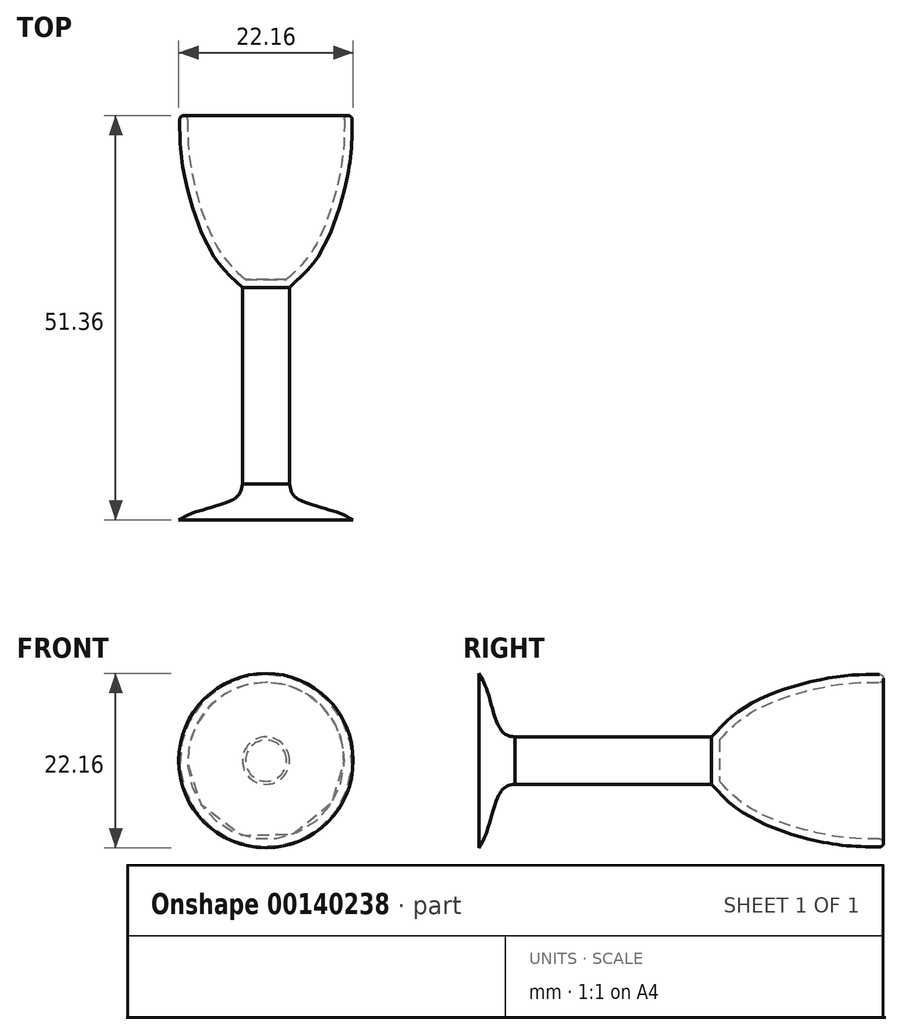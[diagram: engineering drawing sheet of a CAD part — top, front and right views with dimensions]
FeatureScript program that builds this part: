
annotation { "Feature Type Name" : "Feature", "Feature Type Description" : "" }
export const myFeature = defineFeature(function(context is Context, id is Id, definition is map)
    precondition{}
    {
        {
            var Q0;
            Q0=qCreatedBy(makeId("Top.planeOp"),FACE);
            var sketch = newSketch(context, id + "F0", { "sketchPlane" : qUnion([Q0])});
            skLineSegment(sketch, "E0", {"start": v(0, 0) * mm, "end": v(-3, 0) * mm});
            skLineSegment(sketch, "E1", {"start": v(0, 8.3) * mm, "end": v(0, 0) * mm});
            skFitSpline(sketch, "E2", {"points": [v(-3, 0) * mm, v(-6.5, 3.75) * mm, v(-9.46, 10.5) * mm, v(-10.81, 17.24) * mm, v(-10.95, 21.82) * mm], "startDerivative": vector(-15.82, 14.3) * mm, "endDerivative": vector(0.17, 19.93) * mm});
            skLineSegment(sketch, "E3", {"start": v(-10.95, 21.82) * mm, "end": v(0, 21.82) * mm});
            skLineSegment(sketch, "E4", {"start": v(0, 21.82) * mm, "end": v(0, 8.3) * mm});
            skSolve(sketch);
        }
        {
            var Q0;
            Q0=makeQuery(id+"F0.imprint","IMPRINT",FACE,{"disambiguationData":[TD([[makeQuery(id+"F0.imprint","IMPRINT",EDGE,{"derivedFrom":sQuery(id+"F0.wireOp",EDGE,"E0")}),-1.0]])]});
            var Q1;
            Q1=sQuery(id+"F0.wireOp",EDGE,"E1");
            revolve(context, id + "F1", {"entities" : qUnion([Q0]), "axis" : qUnion([Q1]), "revolveType" : RevolveType.FULL});
        }
        {
            var Q0;
            Q0=makeQuery(id+"F1.opRevolve","SWEPT_FACE",FACE,{"disambiguationData":[OSD([sQuery(id+"F0.wireOp",EDGE,"E0")])]});
            var sketch = newSketch(context, id + "F2", { "sketchPlane" : qUnion([Q0])});
            skCircle(sketch, "E5", {"center": v(0, 0) * mm, "radius": 3 * mm});
            skSolve(sketch);
        }
        {
            var Q0;
            Q0=makeQuery(id+"F1.opRevolve","SWEPT_FACE",FACE,{"disambiguationData":[OSD([sQuery(id+"F0.wireOp",EDGE,"E3")])]});
            shell(context, id + "F3", {"entities" : qUnion([Q0]), "thickness" : 1 * mm});
        }
        {
            var Q0;
            Q0=makeQuery(id+"F1.opRevolve","SWEPT_EDGE",EDGE,{"disambiguationData":[OSD([sQuery(id+"F0.wireOp",EDGE,"E2"),sQuery(id+"F0.wireOp",EDGE,"E3")])]});
            var Q1;
            Q1=makeQuery(id+"F3.opShell","OFFSET_EDGE",EDGE,{"disambiguationData":[OSD([sQuery(id+"F0.wireOp",EDGE,"E2"),sQuery(id+"F0.wireOp",EDGE,"E3")])]});
            fillet(context, id + "F4", {"entities" : qUnion([Q0, Q1]), "radius" : .5 * mm, "tangentPropagation" : true, "allowEdgeOverflow" : false});
        }
        {
            var Q0;
            Q0=makeQuery(id+"F2.imprint","IMPRINT",FACE,{"disambiguationData":[TD([[makeQuery(id+"F2.imprint","IMPRINT",EDGE,{"derivedFrom":sQuery(id+"F2.wireOp",EDGE,"E5")}),-1.0]])]});
            extrude(context, id + "F5", {"entities" : qUnion([Q0]), "operationType" : NewBodyOperationType.ADD, "depth" : 25 * mm});
        }
        {
            var Q0;
            Q0=qCreatedBy(makeId("Top.planeOp"),FACE);
            var sketch = newSketch(context, id + "F6", { "sketchPlane" : qUnion([Q0])});
            skLineSegment(sketch, "E6.0", {"start": v(-3, -25) * mm, "end": v(3, -25) * mm});
            skLineSegment(sketch, "E7", {"start": v(0, -25) * mm, "end": v(0, -29.54) * mm});
            skLineSegment(sketch, "E8", {"start": v(0, -29.54) * mm, "end": v(11.08, -29.54) * mm});
            skFitSpline(sketch, "E9", {"points": [v(3, -25) * mm, v(3.76, -26.66) * mm, v(8.66, -28.45) * mm, v(11.08, -29.54) * mm], "startDerivative": vector(1.03, -6.9) * mm, "endDerivative": vector(6.44, -3.54) * mm});
            skSolve(sketch);
        }
        {
            var Q0;
            {var subQ2=sQuery(id+"F6.wireOp",EDGE,"E7");Q0=makeQuery(id+"F6.imprint","IMPRINT",FACE,{"disambiguationData":[TD([[makeQuery(id+"F6.imprint","IMPRINT",EDGE,{"derivedFrom":subQ2}),1.0]])]});}
            var Q1;
            Q1=sQuery(id+"F6.wireOp",EDGE,"E7");
            revolve(context, id + "F7", {"operationType" : NewBodyOperationType.ADD, "entities" : qUnion([Q0]), "axis" : qUnion([Q1]), "revolveType" : RevolveType.FULL});
        }
    });
